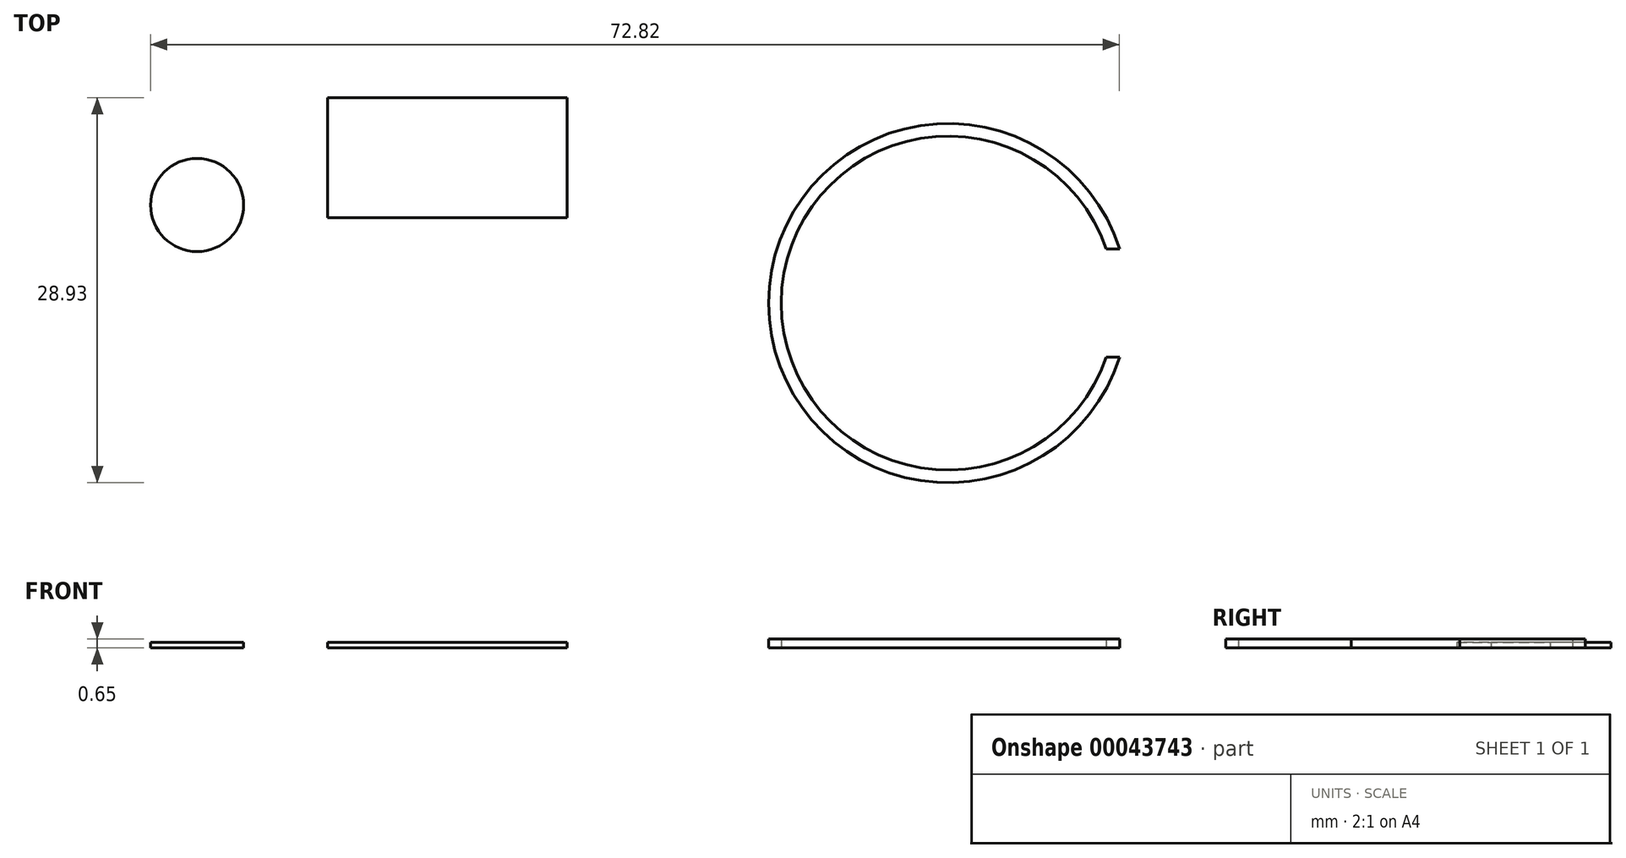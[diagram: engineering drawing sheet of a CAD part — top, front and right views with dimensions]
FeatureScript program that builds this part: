
annotation { "Feature Type Name" : "Feature", "Feature Type Description" : "" }
export const myFeature = defineFeature(function(context is Context, id is Id, definition is map)
    precondition{}
    {
        {
            var Q0;
            Q0=qCreatedBy(makeId("Top.planeOp"),FACE);
            var sketch = newSketch(context, id + "F0", { "sketchPlane" : qUnion([Q0])});
            skCircle(sketch, "E0", {"center": v(-23.37, 19.1) * mm, "radius": 3.5 * mm});
            skLineSegment(sketch, "E1.bottom", {"start": v(-13.56, 27.17) * mm, "end": v(4.44, 27.17) * mm});
            skLineSegment(sketch, "E1.top", {"start": v(-13.56, 18.17) * mm, "end": v(4.44, 18.17) * mm});
            skLineSegment(sketch, "E1.left", {"start": v(-13.56, 27.17) * mm, "end": v(-13.56, 18.17) * mm});
            skLineSegment(sketch, "E1.right", {"start": v(4.44, 27.17) * mm, "end": v(4.44, 18.17) * mm});
            skCircle(sketch, "E2", {"center": v(33.08, 11.74) * mm, "radius": 12.55 * mm});
            skCircle(sketch, "E3", {"center": v(33.08, 11.74) * mm, "radius": 13.5 * mm});
            skLineSegment(sketch, "E4.bottom", {"start": v(44.08, 15.81) * mm, "end": v(47.08, 15.81) * mm});
            skLineSegment(sketch, "E4.top", {"start": v(44.08, 7.66) * mm, "end": v(47.08, 7.66) * mm});
            skPoint(sketch, "E5.visualSharp", {"position": v(47.08, 15.81) * mm});
            skPoint(sketch, "E6.visualSharp", {"position": v(47.08, 7.66) * mm});
            skPoint(sketch, "E7.visualSharp", {"position": v(44.08, 7.66) * mm});
            skPoint(sketch, "E8.visualSharp", {"position": v(44.08, 15.81) * mm});
            skLineSegment(sketch, "E9", {"start": v(47.08, 15.81) * mm, "end": v(47.08, 7.66) * mm});
            skLineSegment(sketch, "E10", {"start": v(44.08, 7.66) * mm, "end": v(44.08, 15.81) * mm});
            skSolve(sketch);
        }
        {
            var Q0;
            Q0=makeQuery(id+"F0.imprint","IMPRINT",FACE,{"disambiguationData":[TD([[makeQuery(id+"F0.imprint","IMPRINT",EDGE,{"derivedFrom":sQuery(id+"F0.wireOp",EDGE,"E0")}),1.0]])]});
            extrude(context, id + "F1", {"entities" : qUnion([Q0]), "depth" : .4 * mm});
        }
        {
            var Q0;
            Q0=makeQuery(id+"F0.imprint","IMPRINT",FACE,{"disambiguationData":[TD([[makeQuery(id+"F0.imprint","IMPRINT",EDGE,{"derivedFrom":sQuery(id+"F0.wireOp",EDGE,"E1.bottom")}),-1.0]])]});
            extrude(context, id + "F2", {"entities" : qUnion([Q0]), "depth" : .4 * mm});
        }
        {
            var Q0;
            {var subQ1=sQuery(id+"F0.wireOp",EDGE,"E2");var subQ5=sQuery(id+"F0.wireOp",EDGE,"E4.bottom");var subQ6=makeQuery(id+"F0.imprint","INTERSECT",VERTEX,{"derivedFrom":[subQ1,subQ5]});Q0=makeQuery(id+"F0.imprint","IMPRINT",FACE,{"disambiguationData":[TD([[makeQuery(id+"F0.imprint","IMPRINT",EDGE,{"disambiguationData":[TD([[subQ6,-1.0]])],"derivedFrom":subQ1}),-1.0]])]});}
            extrude(context, id + "F3", {"entities" : qUnion([Q0]), "depth" : .65 * mm});
        }
    });
